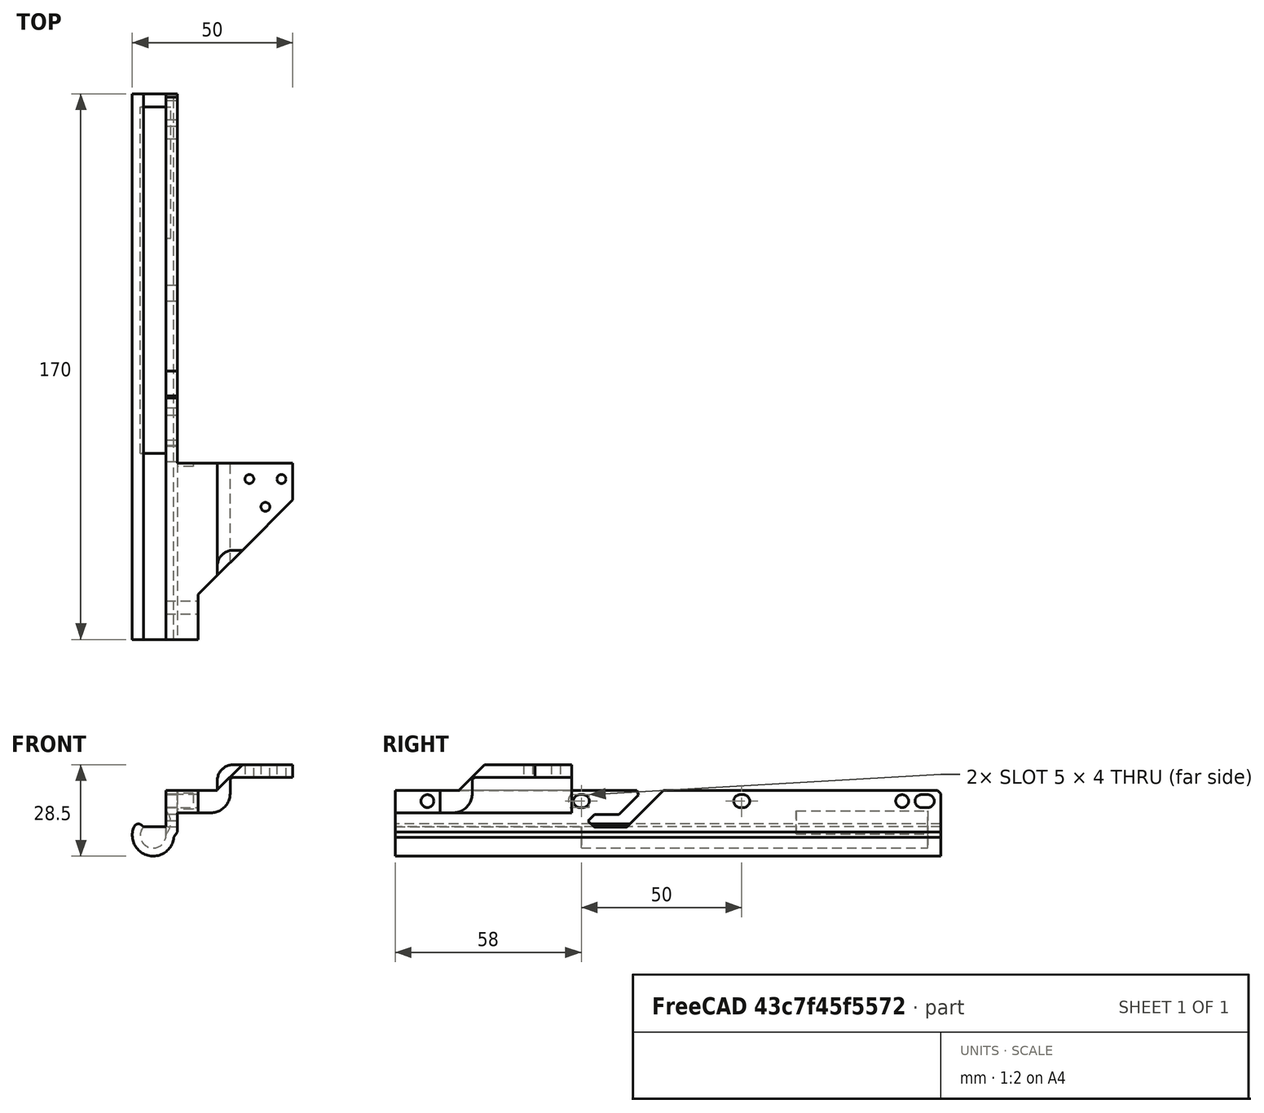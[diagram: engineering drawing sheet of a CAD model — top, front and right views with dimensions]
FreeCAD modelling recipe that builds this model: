
FCSTD DOCUMENT  (FreeCAD 0.19R)
Label: BedChainWire3
License: All rights reserved
LicenseURL: http://en.wikipedia.org/wiki/All_rights_reserved
objects: Sketcher::SketchObject×13, PartDesign::Pocket×8, PartDesign::Pad×5, PartDesign::Fillet×4, PartDesign::Chamfer×2, PartDesign::Body×1, Mesh::Feature×1
note: 52 computed .brp shape members not serialized (recipe doc carries the construction recipe); baked Part::Feature solids carry a one-line shape summary decoded from their .brp

FEATURE [Sketcher::SketchObject] Sketch
  FullyConstrained = true
  MapMode = 5
  Placement = pos=(0,0,0) rot=(1,0,0;1.5708rad)
  Support = -> [XZ_Plane]
  sketch-geometry (6):
    g0: LineSegment StartX=0 StartY=0 StartZ=0 EndX=2.5 EndY=0 EndZ=0
    g1: LineSegment StartX=2.5 StartY=0 StartZ=0 EndX=2.5 EndY=-14 EndZ=0
    g2: ArcOfCircle CenterX=-4 CenterY=-14 CenterZ=0 NormalX=0 NormalY=0 NormalZ=1 AngleXU=0 Radius=4 StartAngle=2.41886 EndAngle=6.28319
    g3: ArcOfCircle CenterX=-4 CenterY=-14 CenterZ=0 NormalX=0 NormalY=0 NormalZ=1 AngleXU=0 Radius=6.5 StartAngle=2.41886 EndAngle=6.28319
    g4: LineSegment StartX=0 StartY=0 StartZ=0 EndX=0 EndY=-14 EndZ=0
    g5: LineSegment StartX=-8.875 StartY=-9.70065 StartZ=0 EndX=-7 EndY=-11.3542 EndZ=0
  constraints (16):
    c: Coincident(g-1,g0)
    c: Horizontal(g0)
    c: Coincident(g0,g1)
    c: Vertical(g1)
    c: Coincident(g3,g2)
    c: Tangent(g3,g1) = 1.5708
    c: Coincident(g4,g0)
    c: Vertical(g4)
    c: Tangent(g4,g2) = 1.5708
    c: Coincident(g5,g3)
    c: Coincident(g5,g2)
    c: Diameter(g2) = 8
    c: Perpendicular(g2,g5)
    c: Distance(g5) = 2.5
    c: Distance(g4) = 14
    c: DistanceX(g2) = -7
FEATURE [PartDesign::Pad] Pad
  Direction = (1,1,1)
  Length = 170
  Length2 = 100
  Placement = pos=(0,0,0) rot=(1,0,0;1.5708rad)
  Profile = -> Sketch
  Type = 0
FEATURE [Sketcher::SketchObject] Sketch001  label="mountHoles"
  FullyConstrained = false
  MapMode = 5
  Placement = pos=(2.5,0,0) rot=(0.707107,0,0.707107;3.14159rad)
  Support = -> [Pad]
  sketch-geometry (14):
    g0: Circle CenterX=-3.35 CenterY=12 CenterZ=0 NormalX=0 NormalY=0 NormalZ=1 AngleXU=0 Radius=2
    g1: Circle CenterX=-3.35 CenterY=160 CenterZ=0 NormalX=0 NormalY=0 NormalZ=1 AngleXU=0 Radius=2
    g2: ArcOfCircle CenterX=-3.35 CenterY=6 CenterZ=0 NormalX=0 NormalY=0 NormalZ=1 AngleXU=0 Radius=2 StartAngle=5e-16 EndAngle=3.14159
    g3: ArcOfCircle CenterX=-3.35 CenterY=4 CenterZ=0 NormalX=0 NormalY=0 NormalZ=1 AngleXU=0 Radius=2 StartAngle=3.14159 EndAngle=6.28319
    g4: LineSegment StartX=-5.35 StartY=6 StartZ=0 EndX=-5.35 EndY=4 EndZ=0
    g5: LineSegment StartX=-1.35 StartY=6 StartZ=0 EndX=-1.35 EndY=4 EndZ=0
    g6: ArcOfCircle CenterX=-3.35 CenterY=112.5 CenterZ=0 NormalX=0 NormalY=0 NormalZ=1 AngleXU=0 Radius=2 StartAngle=1.0821e-12 EndAngle=3.14159
    g7: ArcOfCircle CenterX=-3.35 CenterY=111.5 CenterZ=0 NormalX=0 NormalY=0 NormalZ=1 AngleXU=0 Radius=2 StartAngle=3.14159 EndAngle=6.28319
    g8: LineSegment StartX=-5.35 StartY=112.5 StartZ=0 EndX=-5.35 EndY=111.5 EndZ=0
    g9: LineSegment StartX=-1.35 StartY=112.5 StartZ=0 EndX=-1.35 EndY=111.5 EndZ=0
    g10: ArcOfCircle CenterX=-3.35 CenterY=62.5 CenterZ=0 NormalX=0 NormalY=0 NormalZ=1 AngleXU=0 Radius=2 StartAngle=9e-16 EndAngle=3.14159
    g11: ArcOfCircle CenterX=-3.35 CenterY=61.5 CenterZ=0 NormalX=0 NormalY=0 NormalZ=1 AngleXU=0 Radius=2 StartAngle=3.14159 EndAngle=6.28319
    g12: LineSegment StartX=-5.35 StartY=62.5 StartZ=0 EndX=-5.35 EndY=61.5 EndZ=0
    g13: LineSegment StartX=-1.35 StartY=62.5 StartZ=0 EndX=-1.35 EndY=61.5 EndZ=0
  constraints (35):
    c: DistanceY(g0) = 12
    c: DistanceX(g0) = -3.35
    c: DistanceX(g1) = -3.35
    c: Diameter(g1) = 4
    c: Equal(g1,g0)
    c: Tangent(g2,g5) = 1.5708
    c: Tangent(g2,g4) = -1.5708
    c: Tangent(g4,g3) = -1.5708
    c: Tangent(g5,g3) = 1.5708
    c: Vertical(g4)
    c: Equal(g2,g3)
    c: Distance(g2,g2) = 4
    c: Distance(g2,g3) = 2
    c: DistanceY(g2) = 6
    c: DistanceX(g2) = -3.35
    c: Tangent(g6,g9) = 1.5708
    c: Tangent(g6,g8) = -1.5708
    c: Tangent(g8,g7) = -1.5708
    c: Tangent(g9,g7) = 1.5708
    c: Vertical(g8)
    c: Equal(g6,g7)
    c: Distance(g6,g6) = 4
    c: Distance(g7,g6) = 1
    c: DistanceX(g6) = -3.35
    c: Tangent(g10,g13) = 1.5708
    c: Tangent(g10,g12) = -1.5708
    c: Tangent(g12,g11) = -1.5708
    c: Tangent(g13,g11) = 1.5708
    c: Vertical(g12)
    c: Equal(g10,g11)
    c: Distance(g10,g11) = 1
    c: Distance(g10,g10) = 4
    c: Distance(g0,g10) = 50.5
    c: DistanceX(g10) = -3.35
    c: Distance(g6,g10) = 50
FEATURE [Sketcher::SketchObject] Sketch003  label="chainpad"
  FullyConstrained = true
  MapMode = 5
  Placement = pos=(2.5,0,0) rot=(0.707107,0,0.707107;3.14159rad)
  sketch-geometry (4):
    g0: LineSegment StartX=-7 StartY=170 StartZ=0 EndX=8 EndY=170 EndZ=0
    g1: LineSegment StartX=8 StartY=170 StartZ=0 EndX=8 EndY=115 EndZ=0
    g2: LineSegment StartX=8 StartY=115 StartZ=0 EndX=-7 EndY=115 EndZ=0
    g3: LineSegment StartX=-7 StartY=115 StartZ=0 EndX=-7 EndY=170 EndZ=0
  constraints (12):
    c: Coincident(g0,g1)
    c: Coincident(g1,g2)
    c: Coincident(g2,g3)
    c: Coincident(g3,g0)
    c: Horizontal(g0)
    c: Horizontal(g2)
    c: Vertical(g1)
    c: Vertical(g3)
    c: Distance(g0) = 15
    c: DistanceY(g0) = 170
    c: Distance(g3) = 55
    c: DistanceX(g0) = 8
FEATURE [Sketcher::SketchObject] Sketch004  label="wireExit"
  FullyConstrained = false
  MapMode = 5
  Placement = pos=(2.5,0,0) rot=(0.707107,0,0.707107;3.14159rad)
  sketch-geometry (7):
    g0: LineSegment StartX=-9.5 StartY=109.884 StartZ=0 EndX=-7.5 EndY=107.884 EndZ=0
    g1: LineSegment StartX=-7.5 StartY=107.884 StartZ=0 EndX=-7.5 EndY=100.23 EndZ=0
    g2: LineSegment StartX=-11.5 StartY=97.8841 StartZ=0 EndX=-11.5 EndY=107.884 EndZ=0
    g3: LineSegment StartX=-11.5 StartY=107.884 StartZ=0 EndX=-9.5 EndY=109.884 EndZ=0
    g4: LineSegment StartX=-7.5 StartY=100.23 StartZ=0 EndX=1.8973 EndY=90.8331 EndZ=0
    g5: LineSegment StartX=1.8973 StartY=90.8331 StartZ=0 EndX=4.79463 EndY=81.5895 EndZ=0
    g6: LineSegment StartX=4.79463 StartY=81.5895 StartZ=0 EndX=-11.5 EndY=97.8841 EndZ=0
  constraints (17):
    c: Coincident(g0,g1)
    c: Vertical(g1)
    c: Vertical(g2)
    c: Coincident(g2,g3)
    c: Coincident(g3,g0)
    c: Equal(g3,g0)
    c: Angle(g0) = -0.785398
    c: Distance(g0,g2) = 4
    c: Distance(g2) = 10
    c: DistanceX(g1) = -7.5
    c: Coincident(g1,g4)
    c: Coincident(g4,g5)
    c: Coincident(g5,g6)
    c: Coincident(g6,g2)
    c: Parallel(g6,g4)
    c: Angle(g4) = -0.785398
    c: Perpendicular(g0,g3)
FEATURE [Sketcher::SketchObject] Sketch005  label="chainattachholes"
  FullyConstrained = true
  MapMode = 5
  Placement = pos=(-1.6e-15,1.6e-15,-7) rot=(1,0,0;3.14159rad)
  sketch-geometry (6):
    g0: Circle CenterX=36 CenterY=120 CenterZ=0 NormalX=0 NormalY=0 NormalZ=1 AngleXU=0 Radius=1.4
    g1: Circle CenterX=26 CenterY=120 CenterZ=0 NormalX=0 NormalY=0 NormalZ=1 AngleXU=0 Radius=1.4
    g2: Circle CenterX=31 CenterY=128.66 CenterZ=0 NormalX=0 NormalY=0 NormalZ=1 AngleXU=0 Radius=1.4
    g3: LineSegment StartX=26 StartY=120 StartZ=0 EndX=36 EndY=120 EndZ=0
    g4: LineSegment StartX=36 StartY=120 StartZ=0 EndX=31 EndY=128.66 EndZ=0
    g5: LineSegment StartX=31 StartY=128.66 StartZ=0 EndX=26 EndY=120 EndZ=0
  constraints (15):
    c: Coincident(g3,g1)
    c: Coincident(g3,g0)
    c: Coincident(g3,g4)
    c: Coincident(g4,g2)
    c: Coincident(g4,g5)
    c: Coincident(g5,g3)
    c: Equal(g4,g3)
    c: Equal(g3,g5)
    c: Diameter(g0) = 2.8
    c: Equal(g0,g2)
    c: Equal(g0,g1)
    c: Distance(g3) = 10
    c: Horizontal(g3)
    c: DistanceX(g0) = 36
    c: DistanceY(g0) = 120
FEATURE [Sketcher::SketchObject] Sketch006  label="cableclearance"
  FullyConstrained = true
  MapMode = 5
  Placement = pos=(0,0,0) rot=(-1,0,0;1.5708rad)
  sketch-geometry (2):
    g0: ArcOfCircle CenterX=-3.5 CenterY=10 CenterZ=0 NormalX=0 NormalY=0 NormalZ=1 AngleXU=0 Radius=5 StartAngle=4.71239 EndAngle=7.85398
    g1: LineSegment StartX=-3.5 StartY=15 StartZ=0 EndX=-3.5 EndY=5 EndZ=0
  constraints (7):
    c: Diameter(g0) = 10
    c: DistanceY(g0) = 10
    c: DistanceX(g0) = -3.5
    c: Coincident(g1,g0)
    c: Coincident(g1,g0)
    c: Vertical(g1)
    c: PointOnObject(g0,g1)
FEATURE [Sketcher::SketchObject] Sketch008  label="frontreleif"
  FullyConstrained = false
  MapMode = 5
  Placement = pos=(0,0,1e-15) rot=(0,0,1;3.14159rad)
  sketch-geometry (4):
    g0: LineSegment StartX=-10 StartY=171.39 StartZ=0 EndX=-10 EndY=156 EndZ=0
    g1: LineSegment StartX=-10 StartY=156 StartZ=0 EndX=-54.5867 EndY=111.413 EndZ=0
    g2: LineSegment StartX=-54.5867 StartY=111.413 StartZ=0 EndX=-54.5867 EndY=179.575 EndZ=0
    g3: LineSegment StartX=-54.5867 StartY=179.575 StartZ=0 EndX=-10 EndY=171.39 EndZ=0
  constraints (9):
    c: Vertical(g0)
    c: Coincident(g0,g1)
    c: Coincident(g1,g2)
    c: Vertical(g2)
    c: Coincident(g2,g3)
    c: Coincident(g3,g0)
    c: DistanceX(g0) = -10
    c: DistanceY(g0) = 156
    c: Angle(g1) = -2.35619
FEATURE [Sketcher::SketchObject] Sketch009  label="endcap"
  FullyConstrained = false
  MapMode = 5
  Placement = pos=(0,0,0) rot=(-1,0,0;1.5708rad)
  sketch-geometry (7):
    g0: LineSegment StartX=-8.98889 StartY=11.3212 StartZ=0 EndX=0 EndY=11.3212 EndZ=0
    g1: LineSegment StartX=1.76076 StartY=16.1529 StartZ=0 EndX=-3.18457 EndY=19.1762 EndZ=0
    g2: LineSegment StartX=-3.18457 StartY=19.1762 StartZ=0 EndX=-9.01349 EndY=16.4741 EndZ=0
    g3: LineSegment StartX=-9.01349 StartY=16.4741 StartZ=0 EndX=-8.98889 EndY=11.3212 EndZ=0
    g4: LineSegment StartX=0 StartY=11.3212 StartZ=0 EndX=0 EndY=5.37564 EndZ=0
    g5: LineSegment StartX=0 StartY=5.37564 StartZ=0 EndX=1.76076 EndY=5.37564 EndZ=0
    g6: LineSegment StartX=1.76076 StartY=5.37564 StartZ=0 EndX=1.76076 EndY=16.1529 EndZ=0
  constraints (12):
    c: Horizontal(g0)
    c: Coincident(g1,g2)
    c: Coincident(g2,g3)
    c: Coincident(g3,g0)
    c: PointOnObject(g0,g-2)
    c: Coincident(g0,g4)
    c: PointOnObject(g4,g-2)
    c: Coincident(g4,g5)
    c: Horizontal(g5)
    c: Coincident(g5,g6)
    c: Coincident(g6,g1)
    c: Vertical(g6)
FEATURE [Sketcher::SketchObject] Sketch010  label="frontcap"
  FullyConstrained = false
  MapMode = 5
  Placement = pos=(0,-170,2.26e-13) rot=(1,0,0;1.5708rad)
  sketch-geometry (8):
    g0: LineSegment StartX=1.60772 StartY=-11.3921 StartZ=0 EndX=-8.31304 EndY=-11.3921 EndZ=0
    g1: LineSegment StartX=-8.31304 StartY=-11.3921 StartZ=0 EndX=-9.51489 EndY=-14.3198 EndZ=0
    g2: LineSegment StartX=-9.51489 StartY=-14.3198 StartZ=0 EndX=-8.85866 EndY=-17.0991 EndZ=0
    g3: LineSegment StartX=-8.85866 StartY=-17.0991 StartZ=0 EndX=-6.11791 EndY=-19.2222 EndZ=0
    g4: LineSegment StartX=-6.11791 StartY=-19.2222 StartZ=0 EndX=-3.18414 EndY=-19.2222 EndZ=0
    g5: LineSegment StartX=-3.18414 StartY=-19.2222 StartZ=0 EndX=0.714678 EndY=-18.1028 EndZ=0
    g6: LineSegment StartX=0.714678 StartY=-18.1028 StartZ=0 EndX=1.60772 EndY=-15.7094 EndZ=0
    g7: LineSegment StartX=1.60772 StartY=-15.7094 StartZ=0 EndX=1.60772 EndY=-11.3921 EndZ=0
  constraints (11):
    c: Horizontal(g0)
    c: Coincident(g0,g1)
    c: Coincident(g1,g2)
    c: Coincident(g2,g3)
    c: Coincident(g3,g4)
    c: Horizontal(g4)
    c: Coincident(g4,g5)
    c: Coincident(g5,g6)
    c: Coincident(g6,g7)
    c: Coincident(g7,g0)
    c: Vertical(g7)
FEATURE [Sketcher::SketchObject] Sketch012
  FullyConstrained = false
  MapMode = 5
  Placement = pos=(0,-170,-3.77e-14) rot=(1,0,0;1.5708rad)
  sketch-geometry (4):
    g0: LineSegment StartX=3.5 StartY=0 StartZ=0 EndX=3.5 EndY=-13 EndZ=0
    g1: LineSegment StartX=3.5 StartY=-13 StartZ=0 EndX=0.771706 EndY=-17.3791 EndZ=0
    g2: LineSegment StartX=0.771706 StartY=-17.3791 StartZ=0 EndX=0.771706 EndY=0 EndZ=0
    g3: LineSegment StartX=0.771706 StartY=0 StartZ=0 EndX=3.5 EndY=0 EndZ=0
  constraints (10):
    c: PointOnObject(g0,g-1)
    c: Vertical(g0)
    c: Coincident(g0,g1)
    c: Coincident(g1,g2)
    c: PointOnObject(g2,g-1)
    c: Vertical(g2)
    c: Coincident(g2,g3)
    c: Coincident(g3,g0)
    c: DistanceX(g0) = 3.5
    c: DistanceY(g0) = -13
FEATURE [PartDesign::Pad] Pad001
  BaseFeature = -> Pad
  Direction = (1,1,1)
  Length = 170
  Length2 = 100
  Placement = pos=(0,0,0) rot=(1,0,0;1.5708rad)
  Profile = -> Sketch012
  Reversed = true
  Type = 0
FEATURE [PartDesign::Pad] Pad002
  BaseFeature = -> Pad001
  Direction = (1,1,1)
  Length = 37
  Length2 = 100
  Placement = pos=(0,0,0) rot=(1,0,0;1.5708rad)
  Profile = -> Sketch003
  Type = 0
FEATURE [PartDesign::Pocket] Pocket
  BaseFeature = -> Pad002
  Length = 9
  Length2 = 100
  Placement = pos=(0,0,0) rot=(1,0,0;1.5708rad)
  Profile = -> Sketch008
  Type = 4
FEATURE [Sketcher::SketchObject] Sketch014  label="screwSpace"
  FullyConstrained = false
  MapMode = 5
  Placement = pos=(3.5,0,0) rot=(0.707107,0,0.707107;3.14159rad)
  sketch-geometry (1):
    g0: Circle CenterX=-3.41773 CenterY=112.711 CenterZ=0 NormalX=0 NormalY=0 NormalZ=1 AngleXU=0 Radius=3.33992
FEATURE [Sketcher::SketchObject] Sketch015  label="nozzleNotch"
  FullyConstrained = false
  MapMode = 5
  Placement = pos=(0,-170,-3.77e-14) rot=(1,0,0;1.5708rad)
  Support = -> [Pocket]
  sketch-geometry (10):
    g0: LineSegment StartX=16 StartY=11.6305 StartZ=0 EndX=16 EndY=0 EndZ=0
    g1: LineSegment StartX=16 StartY=0 StartZ=0 EndX=-2.43864 EndY=0 EndZ=0
    g2: LineSegment StartX=-2.43864 StartY=0 StartZ=0 EndX=-2.43864 EndY=11.7877 EndZ=0
    g3: LineSegment StartX=16 StartY=11.6305 StartZ=0 EndX=52.6505 EndY=13.9913 EndZ=0
    g4: LineSegment StartX=52.6505 StartY=13.9913 StartZ=0 EndX=48.5581 EndY=4 EndZ=0
    g5: LineSegment StartX=48.5581 StartY=4 StartZ=0 EndX=20 EndY=4 EndZ=0
    g6: LineSegment StartX=20 StartY=4 StartZ=0 EndX=20 EndY=-9.72327 EndZ=0
    g7: LineSegment StartX=20 StartY=-9.72327 StartZ=0 EndX=64.8225 EndY=-12.0318 EndZ=0
    g8: LineSegment StartX=64.8225 StartY=-12.0318 StartZ=0 EndX=63.0387 EndY=36.5516 EndZ=0
    g9: LineSegment StartX=63.0387 StartY=36.5516 StartZ=0 EndX=-2.43864 EndY=11.7877 EndZ=0
  constraints (19):
    c: Coincident(g0,g1)
    c: Coincident(g1,g2)
    c: Horizontal(g1)
    c: Vertical(g0)
    c: Vertical(g2)
    c: PointOnObject(g0,g-1)
    c: DistanceX(g0) = 16
    c: Coincident(g0,g3)
    c: Coincident(g3,g4)
    c: Coincident(g4,g5)
    c: Coincident(g5,g6)
    c: Vertical(g6)
    c: Coincident(g6,g7)
    c: Coincident(g7,g8)
    c: Coincident(g8,g9)
    c: Coincident(g9,g2)
    c: Distance(g5,g0) = 4
    c: Horizontal(g5)
    c: DistanceY(g5) = 4
FEATURE [Sketcher::SketchObject] Sketch016  label="nosupport"
  FullyConstrained = false
  MapMode = 5
  Placement = pos=(16,0,0) rot=(-0.707107,0,0.707107;3.14159rad)
  sketch-geometry (3):
    g0: LineSegment StartX=-0.125611 StartY=150.048 StartZ=0 EndX=-16.5434 EndY=133.63 EndZ=0
    g1: LineSegment StartX=-16.5434 StartY=133.63 StartZ=0 EndX=-25.8619 EndY=156.859 EndZ=0
    g2: LineSegment StartX=-25.8619 StartY=156.859 StartZ=0 EndX=-0.125611 EndY=150.048 EndZ=0
  constraints (4):
    c: Coincident(g0,g1)
    c: Coincident(g1,g2)
    c: Coincident(g2,g0)
    c: Angle(g0) = -2.35619
FEATURE [PartDesign::Pocket] Pocket001
  BaseFeature = -> Pocket
  Length = 5
  Length2 = 100
  Placement = pos=(0,0,0) rot=(1,0,0;1.5708rad)
  Profile = -> Sketch001
  Type = 4
FEATURE [PartDesign::Pocket] Pocket002
  BaseFeature = -> Pocket001
  Length = 5
  Length2 = 100
  Placement = pos=(0,0,0) rot=(1,0,0;1.5708rad)
  Profile = -> Sketch015
  Type = 1
FEATURE [PartDesign::Pocket] Pocket003
  BaseFeature = -> Pocket002
  Length = 5
  Length2 = 100
  Placement = pos=(0,0,0) rot=(1,0,0;1.5708rad)
  Profile = -> Sketch005
  Type = 1
FEATURE [PartDesign::Fillet] Fillet
  Base = -> Pocket003 [Edge113]
  BaseFeature = -> Pocket003
  Placement = pos=(0,0,0) rot=(1,0,0;1.5708rad)
  Radius = 1
  SupportTransform = false
FEATURE [PartDesign::Pocket] Pocket004
  BaseFeature = -> Fillet
  Length = 5
  Length2 = 100
  Placement = pos=(0,0,0) rot=(1,0,0;1.5708rad)
  Profile = -> Sketch016
  Type = 1
FEATURE [PartDesign::Pad] Pad003
  BaseFeature = -> Pocket004
  Direction = (1,1,1)
  Length = 58
  Length2 = 100
  Placement = pos=(0,0,0) rot=(1,0,0;1.5708rad)
  Profile = -> Sketch010
  Reversed = true
  Type = 0
FEATURE [PartDesign::Pocket] Pocket005
  BaseFeature = -> Pad003
  Length = 5
  Length2 = 100
  Placement = pos=(0,0,0) rot=(1,0,0;1.5708rad)
  Profile = -> Sketch004
  Type = 4
FEATURE [PartDesign::Pocket] Pocket006
  BaseFeature = -> Pocket005
  Length = 5
  Length2 = 100
  Placement = pos=(0,0,0) rot=(1,0,0;1.5708rad)
  Profile = -> Sketch014
  Reversed = true
  Type = 0
FEATURE [PartDesign::Pocket] Pocket007
  BaseFeature = -> Pocket006
  Length = 45
  Length2 = 100
  Placement = pos=(0,0,0) rot=(1,0,0;1.5708rad)
  Profile = -> Sketch006
  Type = 0
FEATURE [PartDesign::Pad] Pad004
  BaseFeature = -> Pocket007
  Direction = (1,1,1)
  Length = 4
  Length2 = 100
  Placement = pos=(0,0,0) rot=(1,0,0;1.5708rad)
  Profile = -> Sketch009
  Reversed = true
  Type = 0
FEATURE [PartDesign::Chamfer] Chamfer
  Angle = 45
  Base = -> Pad004 [Edge76]
  BaseFeature = -> Pad004
  ChamferType = 0
  FlipDirection = false
  Placement = pos=(0,0,0) rot=(1,0,0;1.5708rad)
  Size = 2
  Size2 = 1
  SupportTransform = false
FEATURE [PartDesign::Fillet] Fillet001
  Base = -> Chamfer [Edge138]
  BaseFeature = -> Chamfer
  Placement = pos=(0,0,0) rot=(1,0,0;1.5708rad)
  Radius = 5
  SupportTransform = false
FEATURE [PartDesign::Fillet] Fillet002
  Base = -> Fillet001 [Edge67]
  BaseFeature = -> Fillet001
  Placement = pos=(0,0,0) rot=(1,0,0;1.5708rad)
  Radius = 6
  SupportTransform = false
FEATURE [PartDesign::Chamfer] Chamfer001
  Angle = 45
  Base = -> Fillet002 [Edge169]
  BaseFeature = -> Fillet002
  ChamferType = 0
  FlipDirection = false
  Placement = pos=(0,0,0) rot=(1,0,0;1.5708rad)
  Size = 1
  Size2 = 1
  SupportTransform = false
FEATURE [PartDesign::Fillet] Fillet003
  Base = -> Chamfer001 [Edge132]
  BaseFeature = -> Chamfer001
  Placement = pos=(0,0,0) rot=(1,0,0;1.5708rad)
  Radius = 1.5
  SupportTransform = false
FEATURE [PartDesign::Body] Body
  Group = -> [Sketch,Pad,Sketch001,Sketch003,Sketch004,Sketch005,Sketch006,Sketch008,Sketch009,Sketch010,Sketch012,Pad001,Pad002,Pocket,Sketch014,Sketch015,Sketch016,Pocket001,Pocket002,Pocket003,Fillet,Pocket004,Pad003,Pocket005,Pocket006,Pocket007,Pad004,Chamfer,Fillet001,Fillet002,Chamfer001,Fillet003]
  Origin = -> Origin
  Tip = -> Fillet003
FEATURE [Mesh::Feature] Mesh  label="Fillet003 (Meshed)"
